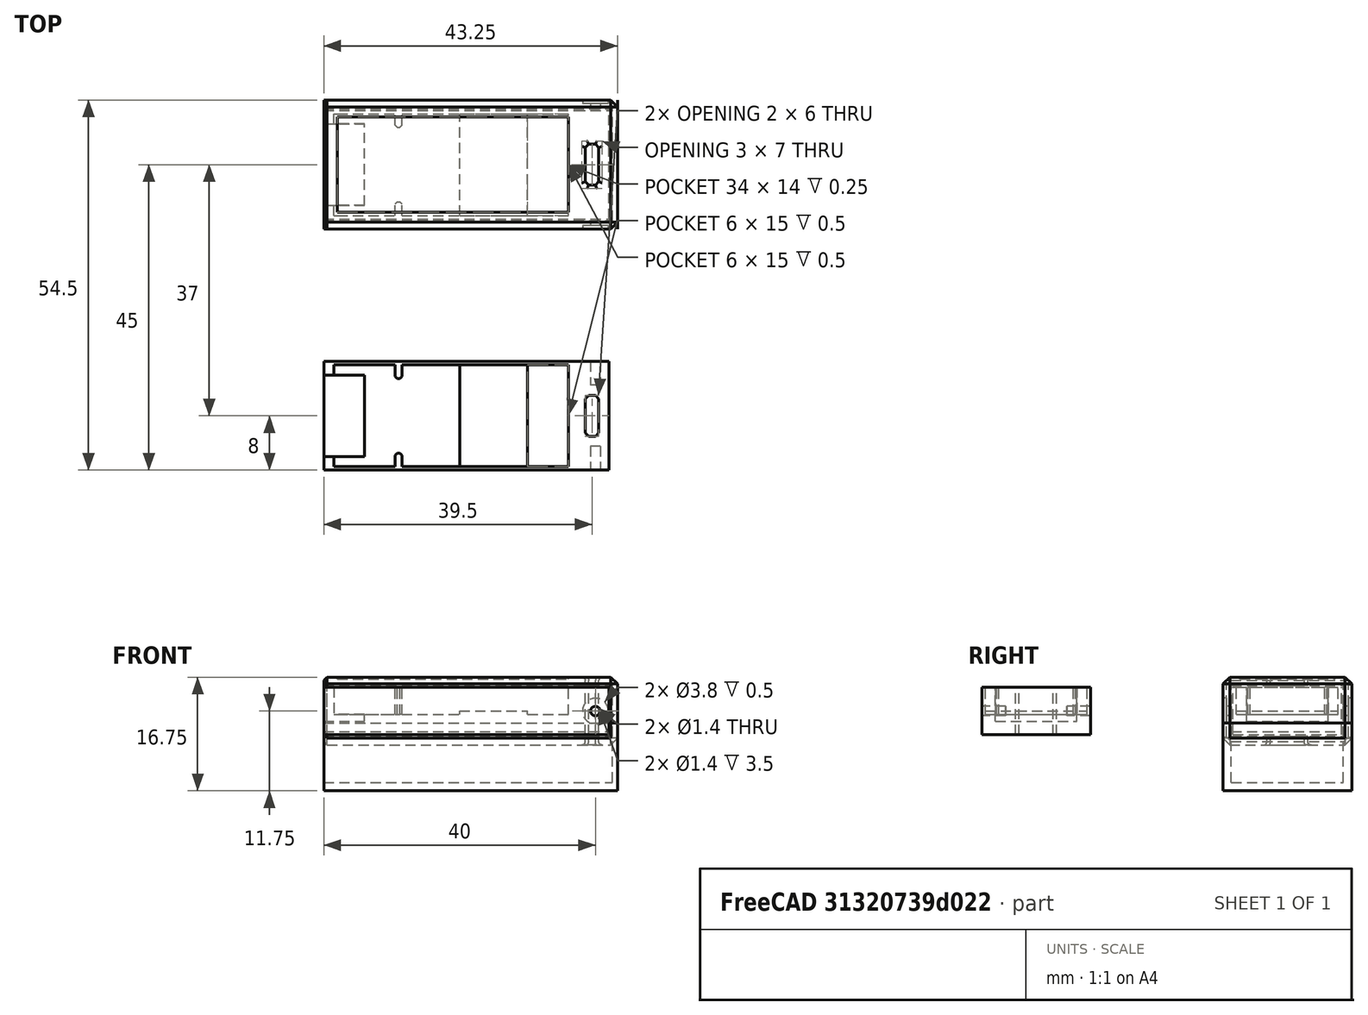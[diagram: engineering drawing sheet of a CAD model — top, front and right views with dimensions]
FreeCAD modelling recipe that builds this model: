
FCSTD DOCUMENT  (FreeCAD 0.18R14555 (Git shallow))
Label: usb
License: All rights reserved
LicenseURL: http://en.wikipedia.org/wiki/All_rights_reserved
objects: Part::Box×12, Part::Cut×9, Part::Chamfer×5, Part::MultiFuse×4, Part::Feature×4, Part::Cylinder×4, Part::Fillet×2
note: 40 computed .brp shape members not serialized (recipe doc carries the construction recipe); baked Part::Feature solids carry a one-line shape summary decoded from their .brp

FEATURE [Part::Box] Box  label="Cube"
  AttacherType = Attacher::AttachEngine3D
  Height = 7
  Length = 37
  Width = 16
FEATURE [Part::Box] Box001  label="Cube001"
  AttacherType = Attacher::AttachEngine3D
  Height = 5
  Length = 6
  Placement = pos=(0,2,2) rot=(0,0,1;0rad)
  Width = 12
FEATURE [Part::Box] Box002  label="Cube002"
  AttacherType = Attacher::AttachEngine3D
  Height = 4
  Length = 34
  Placement = pos=(2,0.5,3) rot=(0,0,1;0rad)
  Width = 15
FEATURE [Part::Box] Box003  label="Cube003"
  AttacherType = Attacher::AttachEngine3D
  Height = 4
  Length = 1
  Placement = pos=(10.5,0.5,3) rot=(0,0,1;0rad)
  Width = 2
FEATURE [Part::Box] Box004  label="Cube004"
  AttacherType = Attacher::AttachEngine3D
  Height = 4
  Length = 1
  Placement = pos=(10.5,13.5,3) rot=(0,0,1;0rad)
  Width = 2
FEATURE [Part::Box] Box005  label="Cube005"
  AttacherType = Attacher::AttachEngine3D
  Height = 0.5
  Length = 10
  Placement = pos=(20,0.5,3) rot=(0,0,1;0rad)
  Width = 15
FEATURE [Part::Cut] Cut
  Base = -> Box
  Tool = -> Box002
FEATURE [Part::Cut] Cut001
  Base = -> Cut
  Tool = -> Box001
FEATURE [Part::Chamfer] Chamfer
  Base = -> Box004
  Edges = 2 edges r=0.3: [Edge1,Edge5]
FEATURE [Part::Chamfer] Chamfer001
  Base = -> Box003
  Edges = 2 edges r=0.3: [Edge3,Edge7]
FEATURE [Part::Box] Box006  label="Cube006"
  AttacherType = Attacher::AttachEngine3D
  Height = 4
  Length = 0.5
  Placement = pos=(1.5,0.5,3) rot=(0,0,1;0rad)
  Width = 15
FEATURE [Part::Cut] Cut002
  Base = -> Cut001
  Tool = -> Box006
FEATURE [Part::MultiFuse] Fusion
  Shapes = -> [Cut002,Chamfer001,Chamfer,Box005]
FEATURE [Part::Box] Box007  label="outer"
  AttacherType = Attacher::AttachEngine3D
  Height = 10
  Length = 43.25
  Placement = pos=(0,-1.5,-1.5) rot=(0,0,1;0rad)
  Width = 19
FEATURE [Part::Box] Box008  label="Cube008"
  AttacherType = Attacher::AttachEngine3D
  Height = 7
  Length = 5
  Placement = pos=(37,0,0) rot=(0,0,1;0rad)
  Width = 16
FEATURE [Part::MultiFuse] Fusion001  label="inner"
  Shapes = -> [Box008,Fusion]
FEATURE [Part::Feature] Fusion001001  label="inner001"
  shape: bbox 42 x 16 x 7 mm, 32 faces (baked)
FEATURE [Part::Box] Box009  label="Cube009"
  AttacherType = Attacher::AttachEngine3D
  Height = 7.5
  Length = 42.5
  Placement = pos=(0,-0.25,-0.25) rot=(0,0,1;0rad)
  Width = 16.5
FEATURE [Part::Cut] Cut003
  Base = -> Box007
  Tool = -> Box009
FEATURE [Part::Feature] Cut003001  label="Cut004"
  Placement = pos=(0,0,-6.75) rot=(0,0,1;0rad)
  shape: bbox 43.25 x 19 x 10 mm, 11 faces (baked)
FEATURE [Part::Cylinder] Cylinder
  Angle = 360
  AttacherType = Attacher::AttachEngine3D
  Height = 5
  Placement = pos=(40,3.5,3.5) rot=(1,0,0;1.5708rad)
  Radius = 0.7
FEATURE [Part::Cylinder] Cylinder001
  Angle = 360
  AttacherType = Attacher::AttachEngine3D
  Height = 5
  Placement = pos=(40,17.5,3.5) rot=(1,0,0;1.5708rad)
  Radius = 0.7
FEATURE [Part::Cylinder] Cylinder002
  Angle = 360
  AttacherType = Attacher::AttachEngine3D
  Height = 0.5
  Placement = pos=(40,17.5,3.5) rot=(1,0,0;1.5708rad)
  Radius = 1.9
FEATURE [Part::Cylinder] Cylinder003
  Angle = 360
  AttacherType = Attacher::AttachEngine3D
  Height = 0.5
  Placement = pos=(40,-1,3.5) rot=(1,0,0;1.5708rad)
  Radius = 1.9
FEATURE [Part::MultiFuse] Fusion001002
  Shapes = -> [Cylinder,Cylinder001]
FEATURE [Part::Feature] Fusion001002001  label="Fusion001003"
  shape: bbox 1.4 x 19 x 1.4 mm, 6 faces, 2 solids (baked)
FEATURE [Part::Cut] Cut003002
  Base = -> Fusion001001
  Tool = -> Fusion001002001
FEATURE [Part::MultiFuse] Fusion001002002
  Shapes = -> [Fusion001002,Cylinder003,Cylinder002]
FEATURE [Part::Cut] Cut003003
  Base = -> Cut003
  Tool = -> Fusion001002002
FEATURE [Part::Box] Box010  label="Cube010"
  AttacherType = Attacher::AttachEngine3D
  Height = 11
  Length = 2
  Placement = pos=(38.5,5,-2) rot=(0,0,1;0rad)
  Width = 6
FEATURE [Part::Chamfer] Chamfer002
  Base = -> Box010
  Edges = 4 edges r=0.5: [Edge1,Edge3,Edge5,Edge7]
FEATURE [Part::Feature] Chamfer002001  label="Chamfer003"
  shape: bbox 2 x 6 x 11 mm, 10 faces (baked)
FEATURE [Part::Cut] Cut003004
  Base = -> Cut003003
  Tool = -> Chamfer002
FEATURE [Part::Cut] Cut003005
  Base = -> Cut003002
  Placement = pos=(0,-37,0) rot=(0,0,1;0rad)
  Tool = -> Chamfer002001
FEATURE [Part::Fillet] Fillet
  Base = -> Cut003004
  Edges = 8 edges r=0.5: [Edge15,Edge16,Edge17,Edge18,Edge19,Edge20,Edge21,Edge22]
FEATURE [Part::Fillet] Fillet001
  Base = -> Fillet
  Edges = 8 edges r=0.5: [Edge59,Edge60,Edge61,Edge62,Edge63,Edge64,Edge65,Edge66]
FEATURE [Part::Chamfer] Chamfer002002
  Base = -> Fillet001
  Edges = 8 edges r=1: [Edge10,Edge11,Edge12,Edge36,Edge37,Edge39,Edge40,Edge42]
FEATURE [Part::Chamfer] Chamfer002003
  Base = -> Chamfer002002
  Edges = 8 edges r=0.5: [Edge1,Edge13,Edge14,Edge15,Edge16,Edge17,Edge18,Edge19]
FEATURE [Part::Box] Box011  label="Cube011"
  AttacherType = Attacher::AttachEngine3D
  Height = 0.25
  Length = 34
  Placement = pos=(2,1,8.25) rot=(0,0,1;0rad)
  Width = 14
FEATURE [Part::Cut] Cut003006
  Base = -> Chamfer002003
  Tool = -> Box011
